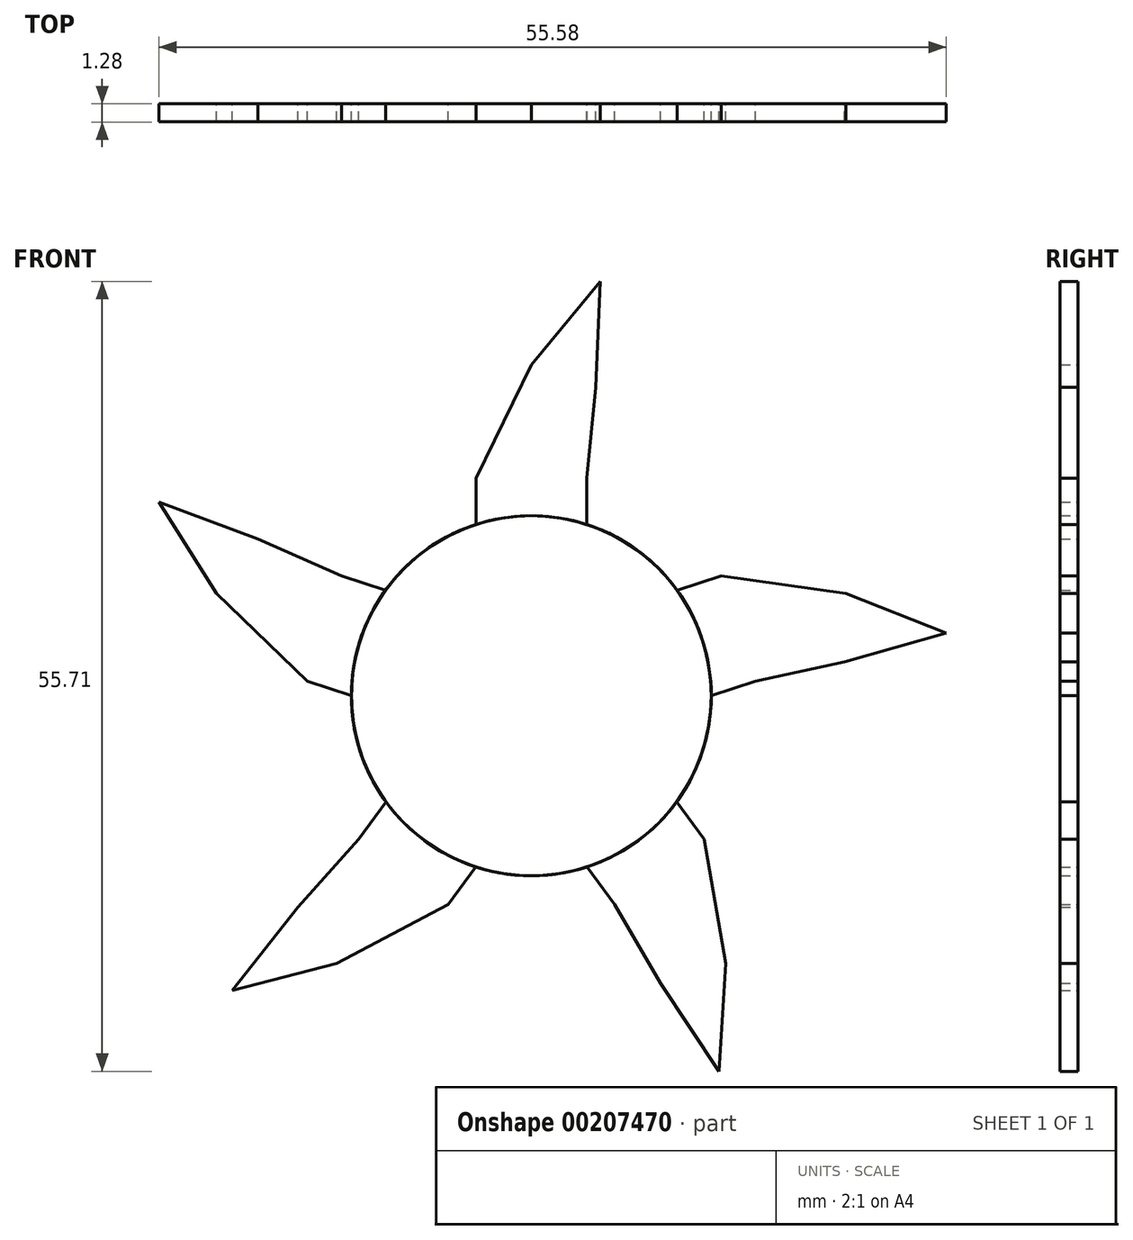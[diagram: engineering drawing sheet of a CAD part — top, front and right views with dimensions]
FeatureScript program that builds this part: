
annotation { "Feature Type Name" : "Feature", "Feature Type Description" : "" }
export const myFeature = defineFeature(function(context is Context, id is Id, definition is map)
    precondition{}
    {
        {
            var Q0;
            Q0=qCreatedBy(makeId("Front.planeOp"),FACE);
            var sketch = newSketch(context, id + "F0", { "sketchPlane" : qUnion([Q0])});
            skCircle(sketch, "E0", {"center": v(0, 0) * mm, "radius": 12.7 * mm});
            skSolve(sketch);
        }
        {
            var Q0;
            Q0=qSketchRegion(id+"F0",true);
            extrude(context, id + "F1", {"entities" : qUnion([Q0]), "endBound" : BoundingType.SYMMETRIC, "depth" : 1.27 * mm});
        }
        {
            var Q0;
            Q0=qCreatedBy(makeId("Front.planeOp"),FACE);
            var sketch = newSketch(context, id + "F2", { "sketchPlane" : qUnion([Q0])});
            skLineSegment(sketch, "E1.bottom", {"start": v(3.9, 15.36) * mm, "end": v(-3.9, 15.36) * mm});
            skLineSegment(sketch, "E1.top", {"start": v(3.9, 9.4) * mm, "end": v(-3.9, 9.4) * mm});
            skLineSegment(sketch, "E1.left", {"start": v(3.9, 15.36) * mm, "end": v(3.9, 9.4) * mm});
            skLineSegment(sketch, "E1.right", {"start": v(-3.9, 15.36) * mm, "end": v(-3.9, 9.4) * mm});
            skPoint(sketch, "E1.middle", {"position": v(0, 12.38) * mm});
            skLineSegment(sketch, "E2", {"start": v(-3.9, 15.36) * mm, "end": v(0, 23.36) * mm});
            skLineSegment(sketch, "E3", {"start": v(0, 23.36) * mm, "end": v(4.55, 21.76) * mm});
            skLineSegment(sketch, "E4", {"start": v(4.55, 21.76) * mm, "end": v(3.9, 15.36) * mm});
            skLineSegment(sketch, "E5", {"start": v(0, 23.36) * mm, "end": v(4.86, 29.22) * mm});
            skLineSegment(sketch, "E6", {"start": v(4.86, 29.22) * mm, "end": v(4.55, 21.76) * mm});
            skSolve(sketch);
        }
        {
            var Q0;
            Q0=qSketchRegion(id+"F2",true);
            extrude(context, id + "F3", {"entities" : qUnion([Q0]), "operationType" : NewBodyOperationType.ADD, "endBound" : BoundingType.SYMMETRIC, "depth" : 1.27 * mm});
        }
        {
            var Q0;
            Q0=makeQuery(id+"F1.opExtrude","SWEPT_BODY",BODY,{"disambiguationData":[OSD([sQuery(id+"F0.wireOp",EDGE,"E0")])]});
            var Q1;
            Q1=sQuery(id+"F0.wireOp",EDGE,"E0");
            circularPattern(context, id + "F4", {"entities" : qUnion([Q0]), "axis" : qUnion([Q1]), "angle" : 360 * degree, "instanceCount" : 5, "equalSpace" : true});
        }
    });
